MODEL slx_427b9d06d6f6
CONFIG AbsTol = auto
CONFIG EnableMultiTasking = off
CONFIG FixedStep = auto
CONFIG MaxStep = auto
CONFIG MinStep = auto
CONFIG RelTol = 1e-3
CONFIG SampleTimeConstraint = Unconstrained
CONFIG SolverName = VariableStepAuto
CONFIG StartTime = 0.0
CONFIG StopTime = 2
BLOCK [Sum] Add
  IconShape = rectangular
  Inputs = +--
  Ports = [3, 1]
BLOCK [Gain] Gain
  Gain = 1/M
BLOCK [Gain] Gain1
  Gain = c1
  NameLocation = top
BLOCK [Gain] Gain2
  Gain = k1
  NameLocation = top
BLOCK [Integrator] Integrator
  Ports = [1, 1]
BLOCK [Integrator] Integrator1
  Ports = [1, 1]
BLOCK [Scope] Scope
  Floating = off
  NumInputPorts = 1
  Ports = [1]
  ScopeSpecificationString = Simulink.scopes.TimeScopeBlockCfg('CurrentConfiguration', extmgr.ConfigurationSet(extmgr.Configuration('Core','General UI',true),extmgr.Configuration('Core','Source UI',true),extmgr.Configuration('Sources','WiredSimulink',true),extmgr.Configuration('Visuals','Time Domain',true,'SerializedDisplays',{struct('MinYLimReal','-0.11464','MaxYLimReal','0.21313','YLabelReal','','MinYLimMag','0.00000','MaxY...<+1430ch>
BLOCK [Scope] Scope1
  Floating = off
  NumInputPorts = 1
  Ports = [1]
  ScopeSpecificationString = Simulink.scopes.TimeScopeBlockCfg('CurrentConfiguration', extmgr.ConfigurationSet(extmgr.Configuration('Core','General UI',true),extmgr.Configuration('Core','Source UI',true),extmgr.Configuration('Sources','WiredSimulink',true,'DataLoggingVariableName','ScopeData1'),extmgr.Configuration('Visuals','Time Domain',true,'SerializedDisplays',{struct('MinYLimReal','-6898.08624','MaxYLimReal','6902.53675'...<+1390ch>
BLOCK [Sin] Sine Wave
  Amplitude = A
  Frequency = omega
  Ports = [0, 1]
  SampleTime = 0
LINE Add:1 -> Gain:1
LINE Gain1:1 -> Add:2
LINE Gain2:1 -> Add:3
LINE Gain:1 -> Integrator:1
LINE Integrator1:1 -> Gain2:1
LINE Integrator1:1 -> Scope:1
LINE Integrator:1 -> Gain1:1
LINE Integrator:1 -> Integrator1:1
LINE Sine Wave:1 -> Add:1
LINE Sine Wave:1 -> Scope1:1
